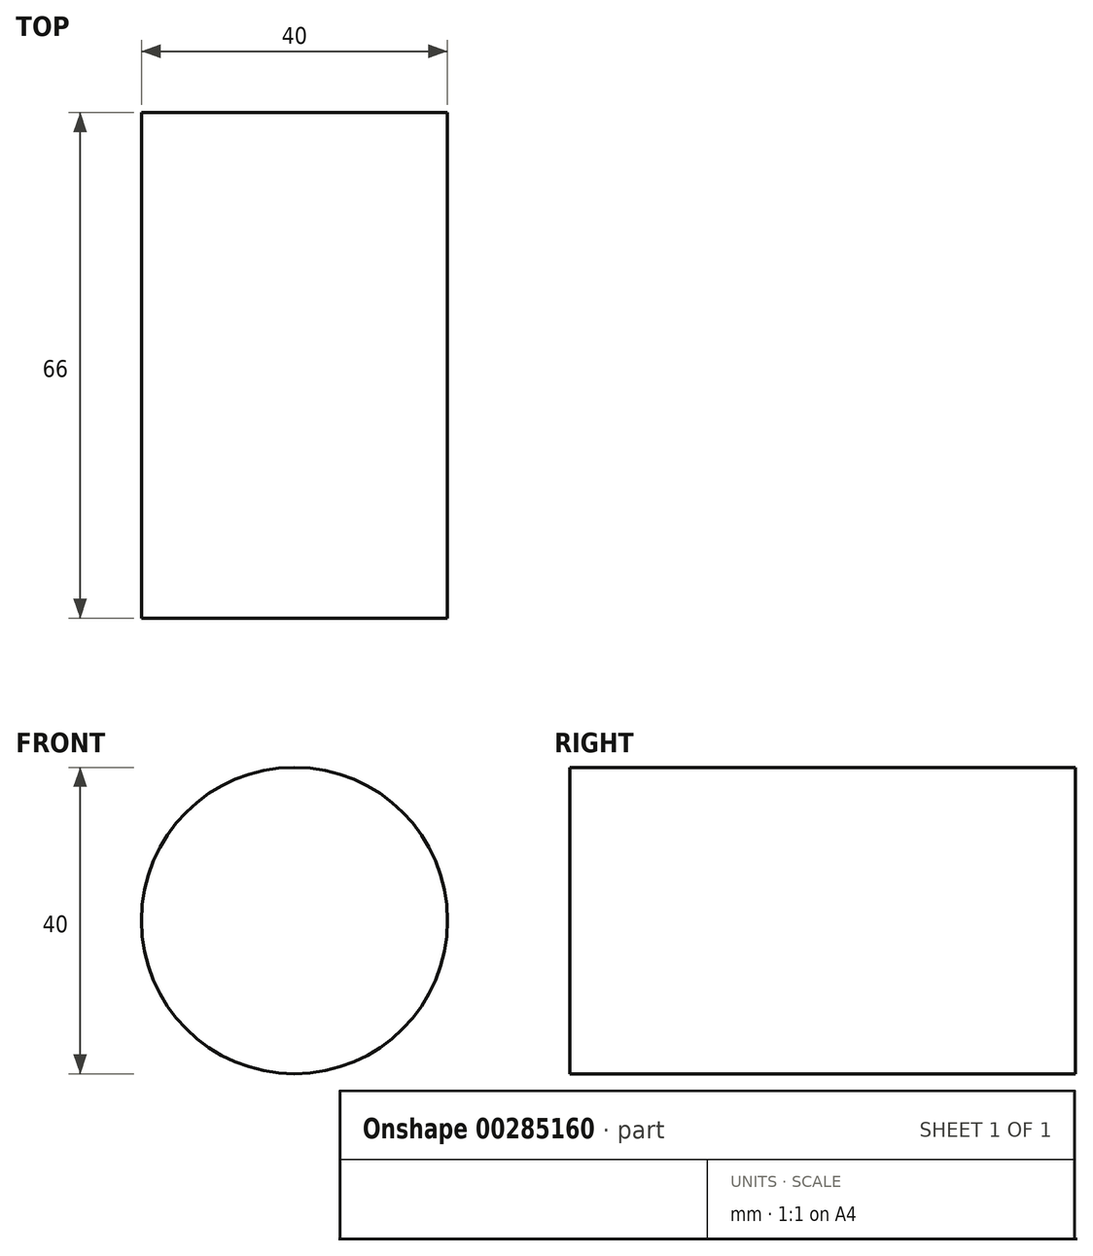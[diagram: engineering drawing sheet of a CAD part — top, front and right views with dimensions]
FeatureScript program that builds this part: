
annotation { "Feature Type Name" : "Feature", "Feature Type Description" : "" }
export const myFeature = defineFeature(function(context is Context, id is Id, definition is map)
    precondition{}
    {
        {
            var Q0;
            Q0=qCreatedBy(makeId("Front.planeOp"),FACE);
            var sketch = newSketch(context, id + "F0", { "sketchPlane" : qUnion([Q0])});
            skCircle(sketch, "E0", {"center": v(0, 0) * mm, "radius": 20 * mm});
            skSolve(sketch);
        }
        {
            var Q0;
            Q0=makeQuery(id+"F0.imprint","IMPRINT",FACE,{"disambiguationData":[TD([[makeQuery(id+"F0.imprint","IMPRINT",EDGE,{"derivedFrom":sQuery(id+"F0.wireOp",EDGE,"E0")}),1.0]])]});
            extrude(context, id + "F1", {"entities" : qUnion([Q0]), "depth" : 66 * mm});
        }
    });
